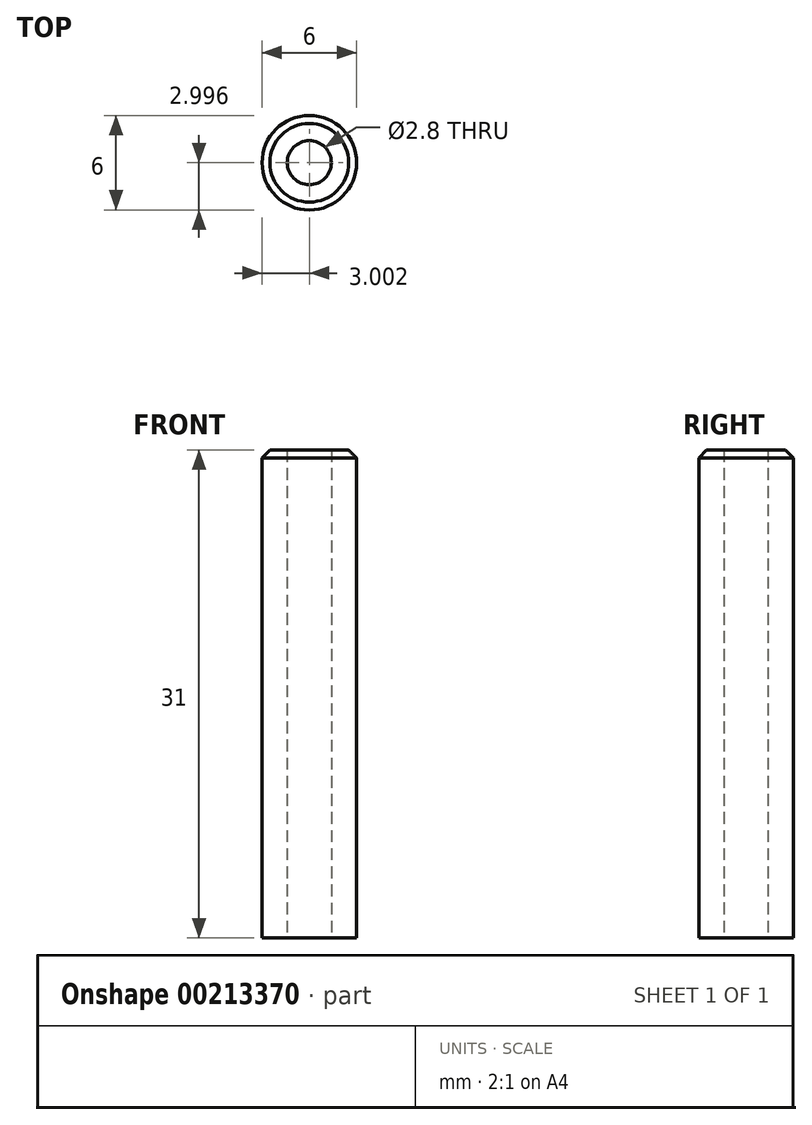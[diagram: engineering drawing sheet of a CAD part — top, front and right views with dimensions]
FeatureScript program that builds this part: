
annotation { "Feature Type Name" : "Feature", "Feature Type Description" : "" }
export const myFeature = defineFeature(function(context is Context, id is Id, definition is map)
    precondition{}
    {
        {
            var Q0;
            Q0=qCreatedBy(makeId("Top.planeOp"),FACE);
            var sketch = newSketch(context, id + "F0", { "sketchPlane" : qUnion([Q0])});
            skCircle(sketch, "E0", {"center": v(-49.94, -23.85) * mm, "radius": 3 * mm});
            skCircle(sketch, "E1", {"center": v(-49.94, -23.85) * mm, "radius": 1.4 * mm});
            skSolve(sketch);
        }
        {
            var Q0;
            Q0=makeQuery(id+"F0.imprint","IMPRINT",FACE,{"disambiguationData":[TD([[makeQuery(id+"F0.imprint","IMPRINT",EDGE,{"derivedFrom":sQuery(id+"F0.wireOp",EDGE,"E0")}),1.0]])]});
            extrude(context, id + "F1", {"entities" : qUnion([Q0]), "depth" : 31 * mm});
        }
        {
            var Q0;
            Q0=makeQuery(id+"F1.opExtrude","CAP_EDGE",EDGE,{"disambiguationData":[OSD([sQuery(id+"F0.wireOp",EDGE,"E0")])],"isStart":false});
            chamfer(context, id + "F2", {"entities" : qUnion([Q0]), "width" : .5 * mm, "tangentPropagation" : true});
        }
    });
